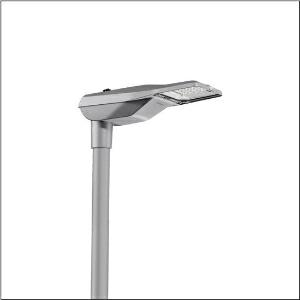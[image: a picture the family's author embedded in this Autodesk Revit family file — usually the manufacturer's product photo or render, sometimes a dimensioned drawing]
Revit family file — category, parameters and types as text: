
# Revit family: streetlight_sl_21_micro___stw1_0a_5xe1e43s08db_ea06
name_source: partatom
category: Lighting Fixtures
units: mm (PartAtom-declared; Revit-internal decimal feet)

## family parameters
Cut with Voids When Loaded = No
Host = Face
Light Source = No
Part Type = Normal
Room Calculation Point = No
Round Connector Dimension = Use Diameter
Shared = No

## types (1)
- --- (1 x LED, 5320 lm, 39.1 W, 4000K)
    Apparent Load = 39 VA
    CIE Flux Codes = 38 75 98 100 100
    Color Rendering = 70
    Color Temperature = 4000K
    Default Elevation = 1800 mm
    Description = Streetlight SL 21 micro, mast luminaire, primary light control with lens, of PMMA, primary optical cover: cover, of toughened safety glass, transparent, light distribution: STW1.0a, light emission: direct distribution, primary light characteristic: asymmetric, installation type: side-entry, post-top, LED, High Power LED, rated luminous flux: 5.320lm, luminous efficacy: 136lm/W, light colour: 740, colour temperature: 4000K, control gear: D4i, control: flexible luminous flux parameterisation, time-dependent luminous flux control, constant luminous flux control, overheat protection, pre-setting: logarithmic dimming characteristic, mains connection: 220..240V, AC, 50/60Hz, start of lifetime: 39W, end of service life: 41W, reduction: 18W, luminaire housing, of diecast aluminium, powder-coated, Siteco® metallic grey (DB 702S), corrosivity category C5 mid according to DIN EN ISO 12944, please order mast flange separately, inclination adjustable: 0°, 5°, 10°, 15°, sealing non-destructively replaceable, multi-level sealing system, length: 528mm, width: 235mm, height: 110mm, mast flange for spigot size: 42mm (side-entry): 5XC10008XM4, 60/48mm (side-entry/post-top): 5XC10108XM2, 76/60mm (side-entry/post-top): 5XC10108XM1, Smart Interface above, protection rating (complete): IP66, insulation class (complete): insulation class II (safety insulation), certification: CE, ENEC, ENEC+, VDE, impact resistance: IK09, permissible operating ambient temperature for outdoor applications: -40..+50°C, standard-compliant lighting for roads and squares, packaging unit: 1 piece

Light Distribution: STW1.0a
    Height = 110 mm
    Lamp = 1 x LED
    Lamp Light Flux = 5320 lm
    Lamp Power = 39.1 W
    Lamp count = 1
    Length = 528 mm
    Luminous efficacy = 136 lm/W
    Manufacturer = Siteco
    ModVariant = No
    Model = 5XE1E43S08DB
    Number of Poles = 1
    OnlyDefault = Yes
    Power Factor = 1
    Product Name = Streetlight SL 21 micro | STW1.0a
    Product group = mast luminaire | pylon top
    ProductGroupID = 6100
    Protection Class = Protection class II
    Protection Degree = IP 66
    RLX_Detail_Level = 1
    RLX_Emergency_Light_Flux = 0 lm
    RLX_Emergency_Type = 0
    RLX_Emergency_Type_DB = No
    RlxData = <blob elided: 98785 chars, md5=97f2b7d2>
    Socket = socket
    Standby Power = 0 W
    System Light Flux = 5320 lm
    System Power = 39 W
    Type Comments = factory setting: luminous flux: 100 % | dim-lin: 254 | 765 mA
    Type Image = l_1277292.jpg
    URL = http://relux.com
    VarID = @adj_150978
    Voltage = 0 V
    Weight = 0.00 kg
    Width = 235 mm

## geometry (parser evidence)
native form markers: Blend x4, Sweep x10
no freeform markers — native parametric forms only
